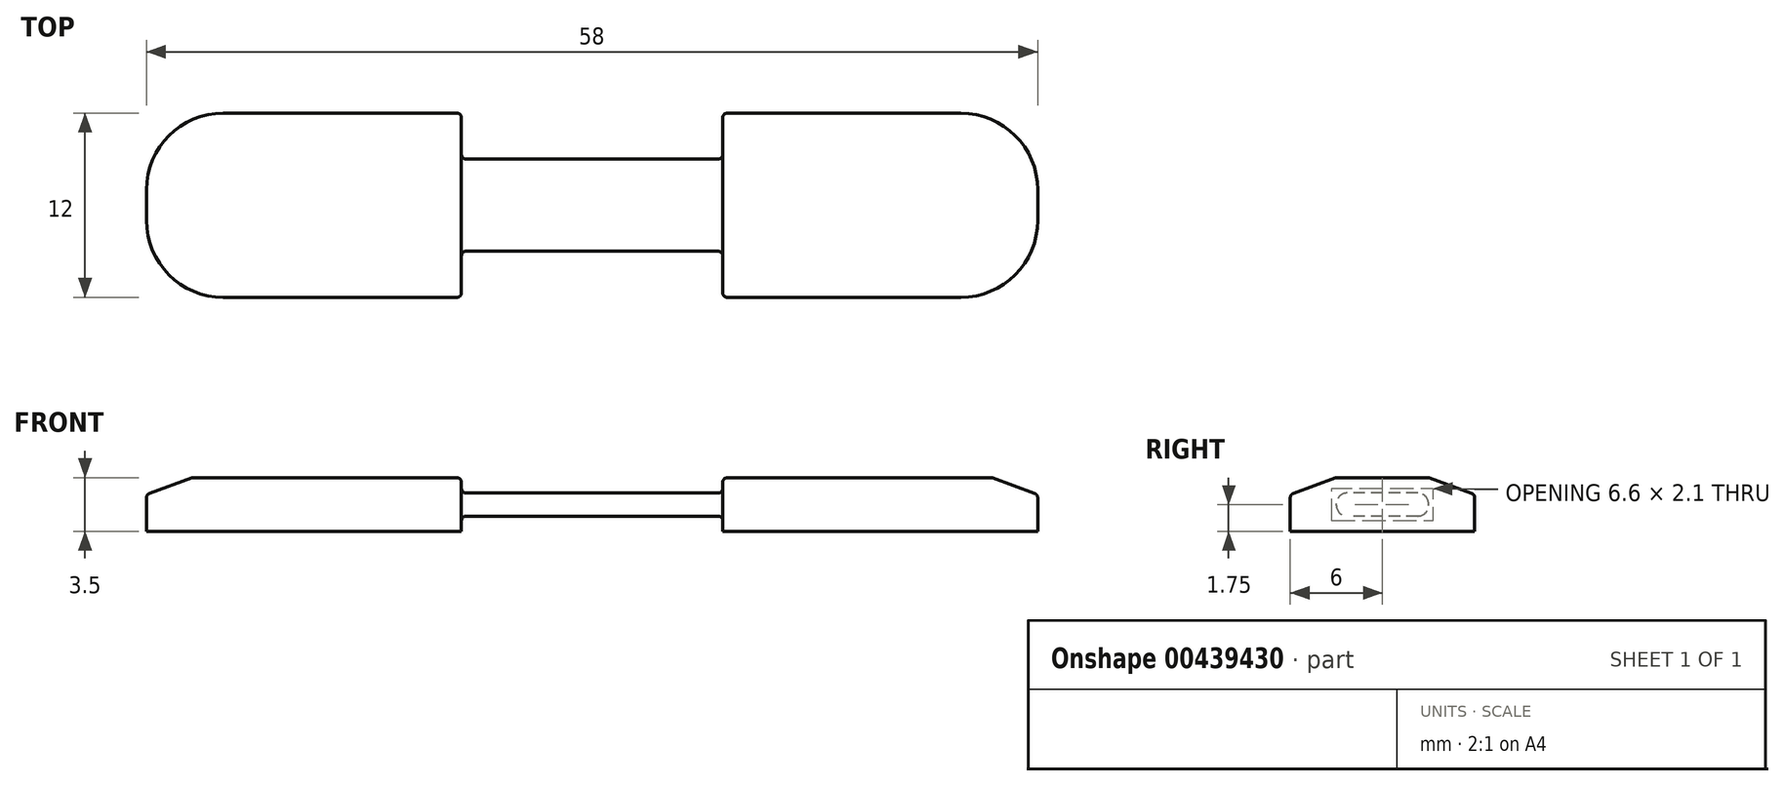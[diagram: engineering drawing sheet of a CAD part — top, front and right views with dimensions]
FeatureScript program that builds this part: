
annotation { "Feature Type Name" : "Feature", "Feature Type Description" : "" }
export const myFeature = defineFeature(function(context is Context, id is Id, definition is map)
    precondition{}
    {
        {
            var Q0;
            Q0=qCreatedBy(makeId("Top.planeOp"),FACE);
            var sketch = newSketch(context, id + "F0", { "sketchPlane" : qUnion([Q0])});
            skLineSegment(sketch, "E0.bottom", {"start": v(-29, 6) * mm, "end": v(29, 6) * mm});
            skLineSegment(sketch, "E0.top", {"start": v(-29, -6) * mm, "end": v(29, -6) * mm});
            skLineSegment(sketch, "E0.left", {"start": v(-29, 6) * mm, "end": v(-29, -6) * mm});
            skLineSegment(sketch, "E0.right", {"start": v(29, 6) * mm, "end": v(29, -6) * mm});
            skPoint(sketch, "E0.middle", {"position": v(0, 0) * mm});
            skSolve(sketch);
        }
        {
            var Q0;
            Q0 = qSketchRegion(id + "F0", true);
            extrude(context, id + "F1", {"entities" : qUnion([Q0]), "depth" : 3.5 * mm});
        }
        {
            var Q0;
            Q0=qCreatedBy(makeId("Right.planeOp"),FACE);
            var sketch = newSketch(context, id + "F2", { "sketchPlane" : qUnion([Q0])});
            skLineSegment(sketch, "E1.bottom", {"start": v(3, 1) * mm, "end": v(-3, 1) * mm});
            skLineSegment(sketch, "E1.top", {"start": v(3, 2.5) * mm, "end": v(-3, 2.5) * mm});
            skLineSegment(sketch, "E1.left", {"start": v(3, 1) * mm, "end": v(3, 2.5) * mm});
            skLineSegment(sketch, "E1.right", {"start": v(-3, 1) * mm, "end": v(-3, 2.5) * mm});
            skPoint(sketch, "E1.middle", {"position": v(0, 1.75) * mm});
            skLineSegment(sketch, "E2", {"start": v(0, 1.75) * mm, "end": v(0, 0) * mm, "construction": true});
            skLineSegment(sketch, "E3.bottom", {"start": v(7, -0.75) * mm, "end": v(-7, -0.75) * mm});
            skLineSegment(sketch, "E3.top", {"start": v(7, 4.25) * mm, "end": v(-7, 4.25) * mm});
            skLineSegment(sketch, "E3.left", {"start": v(7, -0.75) * mm, "end": v(7, 4.25) * mm});
            skLineSegment(sketch, "E3.right", {"start": v(-7, -0.75) * mm, "end": v(-7, 4.25) * mm});
            skSolve(sketch);
        }
        {
            var Q0;
            Q0 = qSketchRegion(id + "F2", true);
            extrude(context, id + "F3", {"entities" : qUnion([Q0]), "operationType" : NewBodyOperationType.REMOVE, "endBound" : BoundingType.SYMMETRIC, "oppositeDirection" : true, "depth" : 17 * mm});
        }
        {
            var Q0;
            Q0=makeQuery(id+"F1.opExtrude","SWEPT_EDGE",EDGE,{"disambiguationData":[OSD([sQuery(id+"F0.wireOp",EDGE,"E0.top"),sQuery(id+"F0.wireOp",EDGE,"E0.right")])]});
            var Q1;
            Q1=makeQuery(id+"F1.opExtrude","SWEPT_EDGE",EDGE,{"disambiguationData":[OSD([sQuery(id+"F0.wireOp",EDGE,"E0.bottom"),sQuery(id+"F0.wireOp",EDGE,"E0.right")])]});
            var Q2;
            Q2=makeQuery(id+"F1.opExtrude","SWEPT_EDGE",EDGE,{"disambiguationData":[OSD([sQuery(id+"F0.wireOp",EDGE,"E0.top"),sQuery(id+"F0.wireOp",EDGE,"E0.left")])]});
            var Q3;
            Q3=makeQuery(id+"F1.opExtrude","SWEPT_EDGE",EDGE,{"disambiguationData":[OSD([sQuery(id+"F0.wireOp",EDGE,"E0.bottom"),sQuery(id+"F0.wireOp",EDGE,"E0.left")])]});
            fillet(context, id + "F4", {"entities" : qUnion([Q0, Q1, Q2, Q3]), "radius" : 5 * mm, "tangentPropagation" : true, "allowEdgeOverflow" : false});
        }
        {
            var Q0;
            {var subQ0=sQuery(id+"F0.wireOp",EDGE,"E0.left");var subQ1=sQuery(id+"F0.wireOp",EDGE,"E0.top");Q0=makeQuery(id+"F3.boolean.opBoolean","SPLIT",EDGE,{"disambiguationData":[TD([makeQuery(id+"F1.opExtrude","SWEPT_FACE",FACE,{"disambiguationData":[OSD([subQ0])]})])],"derivedFrom":makeQuery(id+"F1.opExtrude","CAP_EDGE",EDGE,{"disambiguationData":[OSD([subQ1])],"isStart":false})});}
            var Q1;
            {var subQ0=sQuery(id+"F0.wireOp",EDGE,"E0.right");var subQ1=sQuery(id+"F0.wireOp",EDGE,"E0.top");Q1=makeQuery(id+"F3.boolean.opBoolean","SPLIT",EDGE,{"disambiguationData":[TD([makeQuery(id+"F1.opExtrude","SWEPT_FACE",FACE,{"disambiguationData":[OSD([subQ0])]})])],"derivedFrom":makeQuery(id+"F1.opExtrude","CAP_EDGE",EDGE,{"disambiguationData":[OSD([subQ1])],"isStart":false})});}
            chamfer(context, id + "F5", {"entities" : qUnion([Q0, Q1]), "chamferType" : ChamferType.OFFSET_ANGLE, "width" : 3 * mm, "oppositeDirection" : false, "angle" : 20 * degree, "tangentPropagation" : true});
        }
        {
            var Q0;
            Q0=makeQuery(id+"F3.boolean.opBoolean","COPY",EDGE,{"derivedFrom":makeQuery(id+"F3.opExtrude","SWEPT_EDGE",EDGE,{"disambiguationData":[OSD([sQuery(id+"F2.wireOp",EDGE,"E1.top"),sQuery(id+"F2.wireOp",EDGE,"E1.left")])]})});
            var Q1;
            Q1=makeQuery(id+"F3.boolean.opBoolean","COPY",EDGE,{"derivedFrom":makeQuery(id+"F3.opExtrude","SWEPT_EDGE",EDGE,{"disambiguationData":[OSD([sQuery(id+"F2.wireOp",EDGE,"E1.top"),sQuery(id+"F2.wireOp",EDGE,"E1.right")])]})});
            var Q2;
            Q2=makeQuery(id+"F3.boolean.opBoolean","COPY",EDGE,{"derivedFrom":makeQuery(id+"F3.opExtrude","SWEPT_EDGE",EDGE,{"disambiguationData":[OSD([sQuery(id+"F2.wireOp",EDGE,"E1.bottom"),sQuery(id+"F2.wireOp",EDGE,"E1.right")])]})});
            var Q3;
            Q3=makeQuery(id+"F3.boolean.opBoolean","COPY",EDGE,{"derivedFrom":makeQuery(id+"F3.opExtrude","SWEPT_EDGE",EDGE,{"disambiguationData":[OSD([sQuery(id+"F2.wireOp",EDGE,"E1.bottom"),sQuery(id+"F2.wireOp",EDGE,"E1.left")])]})});
            fillet(context, id + "F6", {"entities" : qUnion([Q0, Q1, Q2, Q3]), "radius" : .7 * mm, "tangentPropagation" : true, "allowEdgeOverflow" : false});
        }
        {
            var Q0;
            Q0=makeQuery(id+"F3.boolean.opBoolean","COPY",EDGE,{"derivedFrom":makeQuery(id+"F3.opExtrude","CAP_EDGE",EDGE,{"disambiguationData":[OSD([sQuery(id+"F2.wireOp",EDGE,"E1.top")])],"isStart":true})});
            var Q1;
            Q1=makeQuery(id+"F3.boolean.opBoolean","COPY",EDGE,{"derivedFrom":makeQuery(id+"F3.opExtrude","CAP_EDGE",EDGE,{"disambiguationData":[OSD([sQuery(id+"F2.wireOp",EDGE,"E1.top")])],"isStart":false})});
            var Q2;
            Q2=makeQuery(id+"F3.boolean.opBoolean","INTERSECT",EDGE,{"derivedFrom":[makeQuery(id+"F1.opExtrude","CAP_FACE",FACE,{"disambiguationData":[OSD([sQuery(id+"F0.wireOp",EDGE,"E0.bottom"),sQuery(id+"F0.wireOp",EDGE,"E0.top"),sQuery(id+"F0.wireOp",EDGE,"E0.left"),sQuery(id+"F0.wireOp",EDGE,"E0.right")])],"isStart":false}),makeQuery(id+"F3.opExtrude","CAP_FACE",FACE,{"disambiguationData":[OSD([sQuery(id+"F2.wireOp",EDGE,"E1.bottom"),sQuery(id+"F2.wireOp",EDGE,"E1.top"),sQuery(id+"F2.wireOp",EDGE,"E1.left"),sQuery(id+"F2.wireOp",EDGE,"E1.right"),sQuery(id+"F2.wireOp",EDGE,"E3.bottom"),sQuery(id+"F2.wireOp",EDGE,"E3.top"),sQuery(id+"F2.wireOp",EDGE,"E3.left"),sQuery(id+"F2.wireOp",EDGE,"E3.right")])],"isStart":false})]});
            var Q3;
            {var subQ0=makeQuery(id+"F3.opExtrude","CAP_FACE",FACE,{"disambiguationData":[OSD([sQuery(id+"F2.wireOp",EDGE,"E1.bottom"),sQuery(id+"F2.wireOp",EDGE,"E1.top"),sQuery(id+"F2.wireOp",EDGE,"E1.left"),sQuery(id+"F2.wireOp",EDGE,"E1.right"),sQuery(id+"F2.wireOp",EDGE,"E3.bottom"),sQuery(id+"F2.wireOp",EDGE,"E3.top"),sQuery(id+"F2.wireOp",EDGE,"E3.left"),sQuery(id+"F2.wireOp",EDGE,"E3.right")])],"isStart":false});var subQ1=sQuery(id+"F0.wireOp",EDGE,"E0.left");var subQ2=sQuery(id+"F0.wireOp",EDGE,"E0.top");Q3=makeQuery(id+"F5.opChamfer","BLEND_EDGE",EDGE,{"blendedFrom":[makeQuery(id+"F3.boolean.opBoolean","SPLIT",EDGE,{"disambiguationData":[TD([makeQuery(id+"F1.opExtrude","SWEPT_FACE",FACE,{"disambiguationData":[OSD([subQ1])]})])],"derivedFrom":makeQuery(id+"F1.opExtrude","CAP_EDGE",EDGE,{"disambiguationData":[OSD([subQ2])],"isStart":false})}),makeQuery(id+"F3.boolean.opBoolean","COPY",FACE,{"derivedFrom":subQ0})],"blendedInto":[makeQuery(id+"F3.boolean.opBoolean","COPY",FACE,{"derivedFrom":subQ0})]});}
            var Q4;
            Q4=makeQuery(id+"F3.boolean.opBoolean","INTERSECT",EDGE,{"derivedFrom":[makeQuery(id+"F1.opExtrude","SWEPT_FACE",FACE,{"disambiguationData":[OSD([sQuery(id+"F0.wireOp",EDGE,"E0.top")])]}),makeQuery(id+"F3.opExtrude","CAP_FACE",FACE,{"disambiguationData":[OSD([sQuery(id+"F2.wireOp",EDGE,"E1.bottom"),sQuery(id+"F2.wireOp",EDGE,"E1.top"),sQuery(id+"F2.wireOp",EDGE,"E1.left"),sQuery(id+"F2.wireOp",EDGE,"E1.right"),sQuery(id+"F2.wireOp",EDGE,"E3.bottom"),sQuery(id+"F2.wireOp",EDGE,"E3.top"),sQuery(id+"F2.wireOp",EDGE,"E3.left"),sQuery(id+"F2.wireOp",EDGE,"E3.right")])],"isStart":false})]});
            var Q5;
            {var subQ0=makeQuery(id+"F3.opExtrude","CAP_FACE",FACE,{"disambiguationData":[OSD([sQuery(id+"F2.wireOp",EDGE,"E1.bottom"),sQuery(id+"F2.wireOp",EDGE,"E1.top"),sQuery(id+"F2.wireOp",EDGE,"E1.left"),sQuery(id+"F2.wireOp",EDGE,"E1.right"),sQuery(id+"F2.wireOp",EDGE,"E3.bottom"),sQuery(id+"F2.wireOp",EDGE,"E3.top"),sQuery(id+"F2.wireOp",EDGE,"E3.left"),sQuery(id+"F2.wireOp",EDGE,"E3.right")])],"isStart":false});var subQ1=sQuery(id+"F0.wireOp",EDGE,"E0.bottom");var subQ2=sQuery(id+"F0.wireOp",EDGE,"E0.left");Q5=makeQuery(id+"F5.opChamfer","BLEND_EDGE",EDGE,{"blendedFrom":[makeQuery(id+"F3.boolean.opBoolean","SPLIT",EDGE,{"disambiguationData":[TD([makeQuery(id+"F1.opExtrude","SWEPT_FACE",FACE,{"disambiguationData":[OSD([subQ2])]})])],"derivedFrom":makeQuery(id+"F1.opExtrude","CAP_EDGE",EDGE,{"disambiguationData":[OSD([subQ1])],"isStart":false})}),makeQuery(id+"F3.boolean.opBoolean","COPY",FACE,{"derivedFrom":subQ0})],"blendedInto":[makeQuery(id+"F3.boolean.opBoolean","COPY",FACE,{"derivedFrom":subQ0})]});}
            var Q6;
            Q6=makeQuery(id+"F3.boolean.opBoolean","INTERSECT",EDGE,{"derivedFrom":[makeQuery(id+"F1.opExtrude","SWEPT_FACE",FACE,{"disambiguationData":[OSD([sQuery(id+"F0.wireOp",EDGE,"E0.bottom")])]}),makeQuery(id+"F3.opExtrude","CAP_FACE",FACE,{"disambiguationData":[OSD([sQuery(id+"F2.wireOp",EDGE,"E1.bottom"),sQuery(id+"F2.wireOp",EDGE,"E1.top"),sQuery(id+"F2.wireOp",EDGE,"E1.left"),sQuery(id+"F2.wireOp",EDGE,"E1.right"),sQuery(id+"F2.wireOp",EDGE,"E3.bottom"),sQuery(id+"F2.wireOp",EDGE,"E3.top"),sQuery(id+"F2.wireOp",EDGE,"E3.left"),sQuery(id+"F2.wireOp",EDGE,"E3.right")])],"isStart":false})]});
            var Q7;
            Q7=makeQuery(id+"F3.boolean.opBoolean","INTERSECT",EDGE,{"derivedFrom":[makeQuery(id+"F1.opExtrude","SWEPT_FACE",FACE,{"disambiguationData":[OSD([sQuery(id+"F0.wireOp",EDGE,"E0.bottom")])]}),makeQuery(id+"F3.opExtrude","CAP_FACE",FACE,{"disambiguationData":[OSD([sQuery(id+"F2.wireOp",EDGE,"E1.bottom"),sQuery(id+"F2.wireOp",EDGE,"E1.top"),sQuery(id+"F2.wireOp",EDGE,"E1.left"),sQuery(id+"F2.wireOp",EDGE,"E1.right"),sQuery(id+"F2.wireOp",EDGE,"E3.bottom"),sQuery(id+"F2.wireOp",EDGE,"E3.top"),sQuery(id+"F2.wireOp",EDGE,"E3.left"),sQuery(id+"F2.wireOp",EDGE,"E3.right")])],"isStart":true})]});
            var Q8;
            {var subQ0=makeQuery(id+"F3.opExtrude","CAP_FACE",FACE,{"disambiguationData":[OSD([sQuery(id+"F2.wireOp",EDGE,"E1.bottom"),sQuery(id+"F2.wireOp",EDGE,"E1.top"),sQuery(id+"F2.wireOp",EDGE,"E1.left"),sQuery(id+"F2.wireOp",EDGE,"E1.right"),sQuery(id+"F2.wireOp",EDGE,"E3.bottom"),sQuery(id+"F2.wireOp",EDGE,"E3.top"),sQuery(id+"F2.wireOp",EDGE,"E3.left"),sQuery(id+"F2.wireOp",EDGE,"E3.right")])],"isStart":true});var subQ1=sQuery(id+"F0.wireOp",EDGE,"E0.bottom");var subQ2=sQuery(id+"F0.wireOp",EDGE,"E0.right");Q8=makeQuery(id+"F5.opChamfer","BLEND_EDGE",EDGE,{"blendedFrom":[makeQuery(id+"F3.boolean.opBoolean","SPLIT",EDGE,{"disambiguationData":[TD([makeQuery(id+"F1.opExtrude","SWEPT_FACE",FACE,{"disambiguationData":[OSD([subQ2])]})])],"derivedFrom":makeQuery(id+"F1.opExtrude","CAP_EDGE",EDGE,{"disambiguationData":[OSD([subQ1])],"isStart":false})}),makeQuery(id+"F3.boolean.opBoolean","COPY",FACE,{"derivedFrom":subQ0})],"blendedInto":[makeQuery(id+"F3.boolean.opBoolean","COPY",FACE,{"derivedFrom":subQ0})]});}
            var Q9;
            Q9=makeQuery(id+"F3.boolean.opBoolean","INTERSECT",EDGE,{"derivedFrom":[makeQuery(id+"F1.opExtrude","CAP_FACE",FACE,{"disambiguationData":[OSD([sQuery(id+"F0.wireOp",EDGE,"E0.bottom"),sQuery(id+"F0.wireOp",EDGE,"E0.top"),sQuery(id+"F0.wireOp",EDGE,"E0.left"),sQuery(id+"F0.wireOp",EDGE,"E0.right")])],"isStart":false}),makeQuery(id+"F3.opExtrude","CAP_FACE",FACE,{"disambiguationData":[OSD([sQuery(id+"F2.wireOp",EDGE,"E1.bottom"),sQuery(id+"F2.wireOp",EDGE,"E1.top"),sQuery(id+"F2.wireOp",EDGE,"E1.left"),sQuery(id+"F2.wireOp",EDGE,"E1.right"),sQuery(id+"F2.wireOp",EDGE,"E3.bottom"),sQuery(id+"F2.wireOp",EDGE,"E3.top"),sQuery(id+"F2.wireOp",EDGE,"E3.left"),sQuery(id+"F2.wireOp",EDGE,"E3.right")])],"isStart":true})]});
            var Q10;
            {var subQ0=makeQuery(id+"F3.opExtrude","CAP_FACE",FACE,{"disambiguationData":[OSD([sQuery(id+"F2.wireOp",EDGE,"E1.bottom"),sQuery(id+"F2.wireOp",EDGE,"E1.top"),sQuery(id+"F2.wireOp",EDGE,"E1.left"),sQuery(id+"F2.wireOp",EDGE,"E1.right"),sQuery(id+"F2.wireOp",EDGE,"E3.bottom"),sQuery(id+"F2.wireOp",EDGE,"E3.top"),sQuery(id+"F2.wireOp",EDGE,"E3.left"),sQuery(id+"F2.wireOp",EDGE,"E3.right")])],"isStart":true});var subQ1=sQuery(id+"F0.wireOp",EDGE,"E0.right");var subQ2=sQuery(id+"F0.wireOp",EDGE,"E0.top");Q10=makeQuery(id+"F5.opChamfer","BLEND_EDGE",EDGE,{"blendedFrom":[makeQuery(id+"F3.boolean.opBoolean","SPLIT",EDGE,{"disambiguationData":[TD([makeQuery(id+"F1.opExtrude","SWEPT_FACE",FACE,{"disambiguationData":[OSD([subQ1])]})])],"derivedFrom":makeQuery(id+"F1.opExtrude","CAP_EDGE",EDGE,{"disambiguationData":[OSD([subQ2])],"isStart":false})}),makeQuery(id+"F3.boolean.opBoolean","COPY",FACE,{"derivedFrom":subQ0})],"blendedInto":[makeQuery(id+"F3.boolean.opBoolean","COPY",FACE,{"derivedFrom":subQ0})]});}
            var Q11;
            Q11=makeQuery(id+"F3.boolean.opBoolean","INTERSECT",EDGE,{"derivedFrom":[makeQuery(id+"F1.opExtrude","SWEPT_FACE",FACE,{"disambiguationData":[OSD([sQuery(id+"F0.wireOp",EDGE,"E0.top")])]}),makeQuery(id+"F3.opExtrude","CAP_FACE",FACE,{"disambiguationData":[OSD([sQuery(id+"F2.wireOp",EDGE,"E1.bottom"),sQuery(id+"F2.wireOp",EDGE,"E1.top"),sQuery(id+"F2.wireOp",EDGE,"E1.left"),sQuery(id+"F2.wireOp",EDGE,"E1.right"),sQuery(id+"F2.wireOp",EDGE,"E3.bottom"),sQuery(id+"F2.wireOp",EDGE,"E3.top"),sQuery(id+"F2.wireOp",EDGE,"E3.left"),sQuery(id+"F2.wireOp",EDGE,"E3.right")])],"isStart":true})]});
            var Q12;
            {var subQ0=sQuery(id+"F0.wireOp",EDGE,"E0.right");var subQ2=sQuery(id+"F0.wireOp",EDGE,"E0.top");var subQ5=makeQuery(id+"F1.opExtrude","SWEPT_FACE",FACE,{"disambiguationData":[OSD([subQ0])]});var subQ7=makeQuery(id+"F1.opExtrude","SWEPT_FACE",FACE,{"disambiguationData":[OSD([subQ2])]});Q12=makeQuery(id+"F5.opChamfer","BLEND_EDGE",EDGE,{"blendedFrom":[makeQuery(id+"F3.boolean.opBoolean","SPLIT",EDGE,{"disambiguationData":[TD([subQ5])],"derivedFrom":makeQuery(id+"F1.opExtrude","CAP_EDGE",EDGE,{"disambiguationData":[OSD([subQ2])],"isStart":false})}),makeQuery(id+"F3.boolean.opBoolean","SPLIT",FACE,{"disambiguationData":[TD([subQ5])],"derivedFrom":subQ7})],"blendedInto":[makeQuery(id+"F3.boolean.opBoolean","SPLIT",FACE,{"disambiguationData":[TD([subQ5])],"derivedFrom":subQ7})]});}
            var Q13;
            {var subQ0=sQuery(id+"F0.wireOp",EDGE,"E0.bottom");var subQ1=sQuery(id+"F0.wireOp",EDGE,"E0.right");var subQ2=sQuery(id+"F0.wireOp",EDGE,"E0.top");var subQ3=makeQuery(id+"F3.boolean.opBoolean","SPLIT",FACE,{"disambiguationData":[TD([makeQuery(id+"F1.opExtrude","SWEPT_FACE",FACE,{"disambiguationData":[OSD([subQ1])]})])],"derivedFrom":makeQuery(id+"F1.opExtrude","CAP_FACE",FACE,{"disambiguationData":[OSD([subQ0,subQ2,sQuery(id+"F0.wireOp",EDGE,"E0.left"),subQ1])],"isStart":false})});Q13=makeQuery(id+"F5.opChamfer","BLEND_EDGE",EDGE,{"blendedFrom":[makeQuery(id+"F4.opFillet","BLEND_EDGE",EDGE,{"blendedFrom":[makeQuery(id+"F1.opExtrude","SWEPT_EDGE",EDGE,{"disambiguationData":[OSD([subQ2,subQ1])]}),subQ3],"blendedInto":[subQ3]}),subQ3],"blendedInto":[subQ3]});}
            var Q14;
            {var subQ0=sQuery(id+"F0.wireOp",EDGE,"E0.bottom");var subQ1=sQuery(id+"F0.wireOp",EDGE,"E0.top");var subQ2=sQuery(id+"F0.wireOp",EDGE,"E0.left");var subQ3=makeQuery(id+"F3.boolean.opBoolean","SPLIT",FACE,{"disambiguationData":[TD([makeQuery(id+"F1.opExtrude","SWEPT_FACE",FACE,{"disambiguationData":[OSD([subQ2])]})])],"derivedFrom":makeQuery(id+"F1.opExtrude","CAP_FACE",FACE,{"disambiguationData":[OSD([subQ0,subQ1,subQ2,sQuery(id+"F0.wireOp",EDGE,"E0.right")])],"isStart":false})});Q14=makeQuery(id+"F5.opChamfer","BLEND_EDGE",EDGE,{"blendedFrom":[makeQuery(id+"F4.opFillet","BLEND_EDGE",EDGE,{"blendedFrom":[makeQuery(id+"F1.opExtrude","SWEPT_EDGE",EDGE,{"disambiguationData":[OSD([subQ1,subQ2])]}),subQ3],"blendedInto":[subQ3]}),subQ3],"blendedInto":[subQ3]});}
            var Q15;
            {var subQ0=sQuery(id+"F0.wireOp",EDGE,"E0.left");var subQ1=sQuery(id+"F0.wireOp",EDGE,"E0.top");var subQ2=sQuery(id+"F0.wireOp",EDGE,"E0.bottom");Q15=makeQuery(id+"F5.opChamfer","BLEND_EDGE",EDGE,{"blendedFrom":[makeQuery(id+"F4.opFillet","BLEND_EDGE",EDGE,{"blendedFrom":[makeQuery(id+"F1.opExtrude","SWEPT_EDGE",EDGE,{"disambiguationData":[OSD([subQ1,subQ0])]}),makeQuery(id+"F3.boolean.opBoolean","SPLIT",FACE,{"disambiguationData":[TD([makeQuery(id+"F1.opExtrude","SWEPT_FACE",FACE,{"disambiguationData":[OSD([subQ0])]})])],"derivedFrom":makeQuery(id+"F1.opExtrude","CAP_FACE",FACE,{"disambiguationData":[OSD([subQ2,subQ1,subQ0,sQuery(id+"F0.wireOp",EDGE,"E0.right")])],"isStart":false})})],"blendedInto":[makeQuery(id+"F3.boolean.opBoolean","SPLIT",FACE,{"disambiguationData":[TD([makeQuery(id+"F1.opExtrude","SWEPT_FACE",FACE,{"disambiguationData":[OSD([subQ0])]})])],"derivedFrom":makeQuery(id+"F1.opExtrude","CAP_FACE",FACE,{"disambiguationData":[OSD([subQ2,subQ1,subQ0,sQuery(id+"F0.wireOp",EDGE,"E0.right")])],"isStart":false})})]}),makeQuery(id+"F4.opFillet","BLEND_FACE",FACE,{"disambiguationData":[OSD([subQ1,subQ0])]})],"blendedInto":[makeQuery(id+"F4.opFillet","BLEND_FACE",FACE,{"disambiguationData":[OSD([subQ1,subQ0])]})]});}
            fillet(context, id + "F7", {"entities" : qUnion([Q0, Q1, Q2, Q3, Q4, Q5, Q6, Q7, Q8, Q9, Q10, Q11, Q12, Q13, Q14, Q15]), "radius" : .3 * mm, "tangentPropagation" : true, "allowEdgeOverflow" : false});
        }
    });
